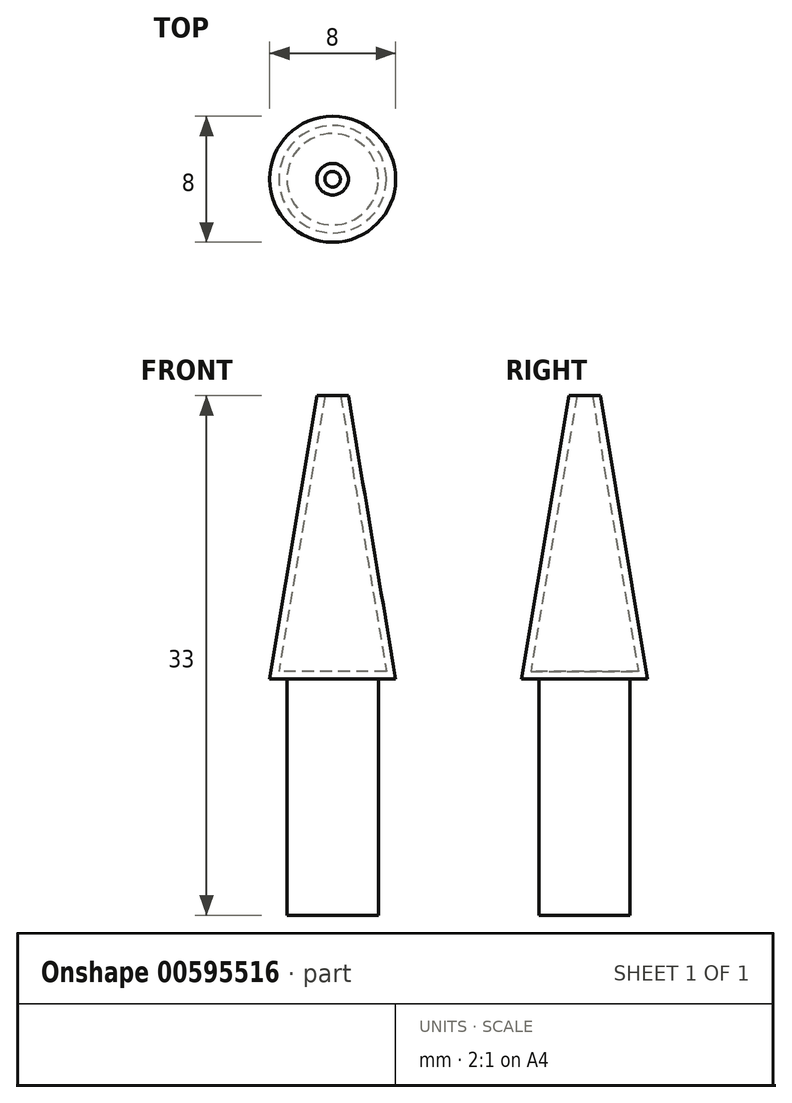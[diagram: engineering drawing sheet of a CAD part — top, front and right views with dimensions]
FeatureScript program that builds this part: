
annotation { "Feature Type Name" : "Feature", "Feature Type Description" : "" }
export const myFeature = defineFeature(function(context is Context, id is Id, definition is map)
    precondition{}
    {
        {
            var Q0;
            Q0=qCreatedBy(makeId("Top.planeOp"),FACE);
            var sketch = newSketch(context, id + "F0", { "sketchPlane" : qUnion([Q0])});
            skCircle(sketch, "E0", {"center": v(0, 0) * mm, "radius": 4 * mm});
            skSolve(sketch);
        }
        {
            var Q0;
            Q0=qCreatedBy(makeId("Top.planeOp"),FACE);
            cPlane(context, id + "F1", {"entities" : qUnion([Q0]), "cplaneType" : CPlaneType.OFFSET, "offset" : 18 * mm, "width" : 150 * mm, "height" : 150 * mm});
        }
        {
            var Q0;
            Q0=qCreatedBy(id+"F1.planeOp",FACE);
            var sketch = newSketch(context, id + "F2", { "sketchPlane" : qUnion([Q0])});
            skCircle(sketch, "E1", {"center": v(0, 0) * mm, "radius": 1 * mm});
            skSolve(sketch);
        }
        {
            var Q0;
            Q0=makeQuery(id+"F0.imprint","IMPRINT",FACE,{"disambiguationData":[TD([[makeQuery(id+"F0.imprint","IMPRINT",EDGE,{"derivedFrom":sQuery(id+"F0.wireOp",EDGE,"E0")}),1.0]])]});
            var Q1;
            Q1=makeQuery(id+"F2.imprint","IMPRINT",FACE,{"disambiguationData":[TD([[makeQuery(id+"F2.imprint","IMPRINT",EDGE,{"derivedFrom":sQuery(id+"F2.wireOp",EDGE,"E1")}),1.0]])]});
            loft(context, id + "F3", {"sheetProfilesArray" : [{ "sheetProfileEntities" : qUnion([Q0]) }, { "sheetProfileEntities" : qUnion([Q1]) }]});
        }
        {
            var Q0;
            Q0=makeQuery(id+"F3.opLoft","CAP_FACE",FACE,{"disambiguationData":[OSD([makeQuery(id+"F2.imprint","IMPRINT",FACE,{"disambiguationData":[TD([[makeQuery(id+"F2.imprint","IMPRINT",EDGE,{"derivedFrom":sQuery(id+"F2.wireOp",EDGE,"E1")}),1.0]])]})])],"isStart":true});
            shell(context, id + "F4", {"entities" : qUnion([Q0]), "thickness" : 0.5 * mm});
        }
        {
            var Q0;
            Q0=makeQuery(id+"F3.opLoft","CAP_FACE",FACE,{"disambiguationData":[OSD([makeQuery(id+"F0.imprint","IMPRINT",FACE,{"disambiguationData":[TD([[makeQuery(id+"F0.imprint","IMPRINT",EDGE,{"derivedFrom":sQuery(id+"F0.wireOp",EDGE,"E0")}),1.0]])]})])],"isStart":true});
            var sketch = newSketch(context, id + "F5", { "sketchPlane" : qUnion([Q0])});
            skCircle(sketch, "E2", {"center": v(0, 0) * mm, "radius": 2.9 * mm});
            skSolve(sketch);
        }
        {
            var Q0;
            Q0=makeQuery(id+"F5.imprint","IMPRINT",FACE,{"disambiguationData":[TD([[makeQuery(id+"F5.imprint","IMPRINT",EDGE,{"derivedFrom":sQuery(id+"F5.wireOp",EDGE,"E2")}),1.0]])]});
            extrude(context, id + "F6", {"entities" : qUnion([Q0]), "operationType" : NewBodyOperationType.ADD, "depth" : 15 * mm, "offsetDistance" : 25 * mm});
        }
    });
